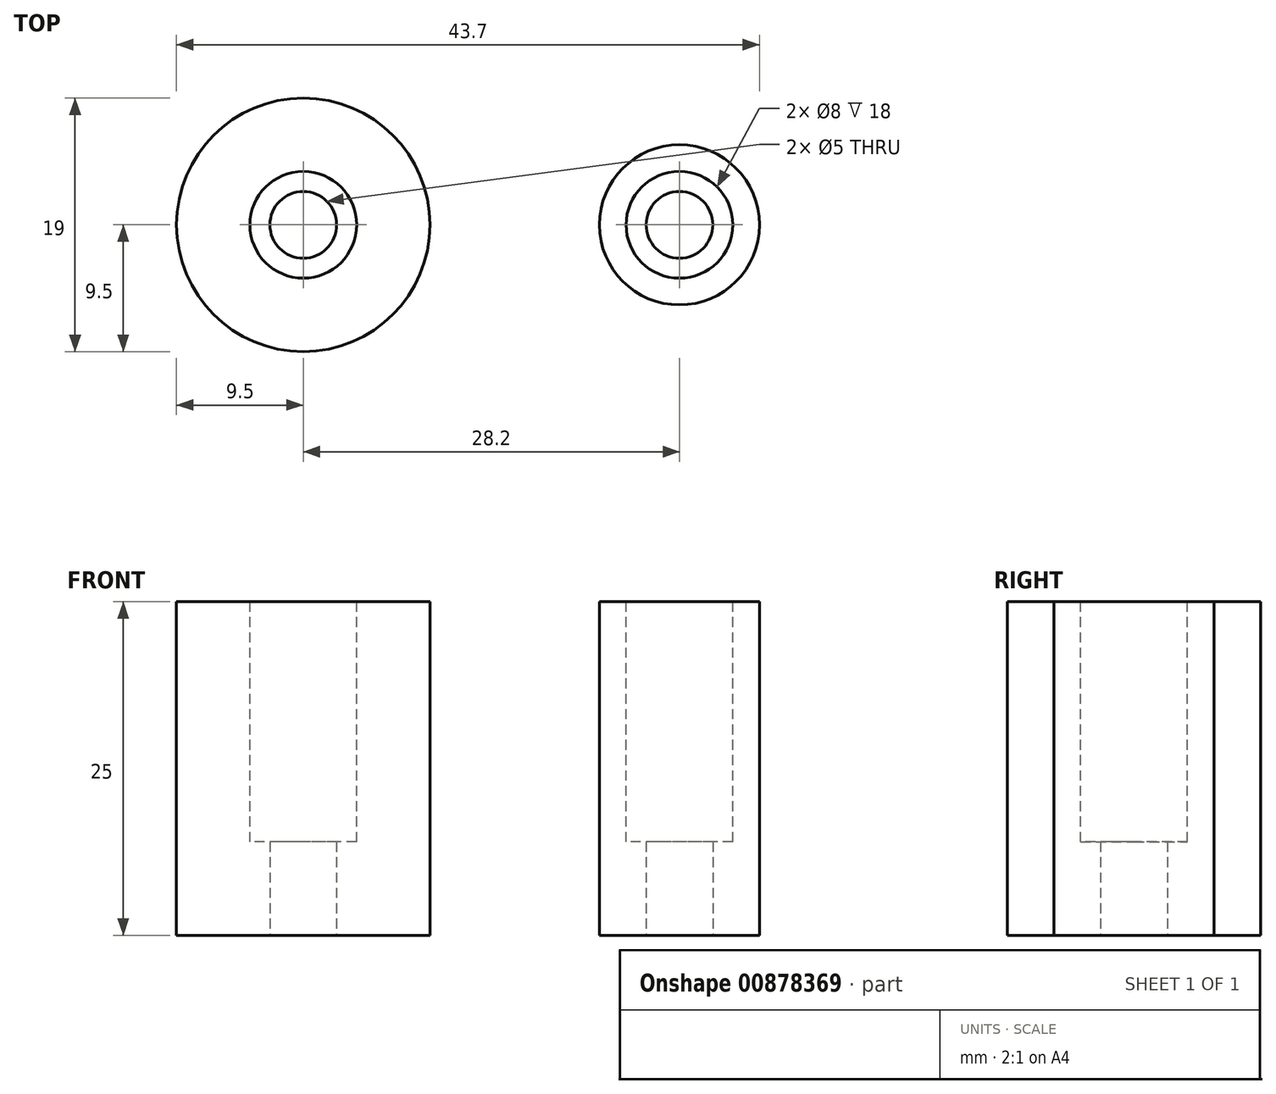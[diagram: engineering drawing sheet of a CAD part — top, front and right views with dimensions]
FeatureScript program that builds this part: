
annotation { "Feature Type Name" : "Feature", "Feature Type Description" : "" }
export const myFeature = defineFeature(function(context is Context, id is Id, definition is map)
    precondition{}
    {
        {
            var Q0;
            Q0=qCreatedBy(makeId("Top.planeOp"),FACE);
            var sketch = newSketch(context, id + "F0", { "sketchPlane" : qUnion([Q0])});
            skCircle(sketch, "E0", {"center": v(0, 0) * mm, "radius": 9.5 * mm});
            skSolve(sketch);
        }
        {
            var Q0;
            Q0 = qSketchRegion(id + "F0", true);
            extrude(context, id + "F1", {"entities" : qUnion([Q0]), "depth" : 25 * mm, "offsetDistance" : 25 * mm});
        }
        {
            var Q0;
            Q0=makeQuery(id+"F1.opExtrude","CAP_FACE",FACE,{"disambiguationData":[OSD([sQuery(id+"F0.wireOp",EDGE,"E0")])],"isStart":false});
            var sketch = newSketch(context, id + "F2", { "sketchPlane" : qUnion([Q0])});
            skCircle(sketch, "E1", {"center": v(0, 0) * mm, "radius": 4 * mm});
            skSolve(sketch);
        }
        {
            var Q0;
            Q0 = qSketchRegion(id + "F2", true);
            extrude(context, id + "F3", {"entities" : qUnion([Q0]), "operationType" : NewBodyOperationType.REMOVE, "oppositeDirection" : true, "depth" : 18 * mm, "offsetDistance" : 25 * mm});
        }
        {
            var Q0;
            Q0=makeQuery(id+"F1.opExtrude","CAP_FACE",FACE,{"disambiguationData":[OSD([sQuery(id+"F0.wireOp",EDGE,"E0")])],"isStart":true});
            var sketch = newSketch(context, id + "F4", { "sketchPlane" : qUnion([Q0])});
            skCircle(sketch, "E2", {"center": v(0, 0) * mm, "radius": 2.5 * mm});
            skSolve(sketch);
        }
        {
            var Q0;
            Q0 = qSketchRegion(id + "F4", true);
            extrude(context, id + "F5", {"entities" : qUnion([Q0]), "operationType" : NewBodyOperationType.REMOVE, "oppositeDirection" : true, "depth" : 25 * mm, "offsetDistance" : 25 * mm});
        }
        {
            var Q0;
            Q0=makeQuery(id+"F1.opExtrude","SWEPT_BODY",BODY,{"disambiguationData":[OSD([sQuery(id+"F0.wireOp",EDGE,"E0")])]});
            transform(context, id + "F6", {"entities" : qUnion([Q0]), "transformType" : TransformType.TRANSLATION_3D, "dx" : 28.2 * mm, "dy" : 0 * mm, "dz" : 0 * mm, "makeCopy" : true});
        }
        {
            var Q0;
            Q0=makeQuery(id+"F6.opPattern","COPY",FACE,{"derivedFrom":makeQuery(id+"F1.opExtrude","CAP_FACE",FACE,{"disambiguationData":[OSD([sQuery(id+"F0.wireOp",EDGE,"E0")])],"isStart":false}),"instanceName":"1"});
            var sketch = newSketch(context, id + "F7", { "sketchPlane" : qUnion([Q0])});
            skCircle(sketch, "E3", {"center": v(28.2, 0) * mm, "radius": 6 * mm});
            skSolve(sketch);
        }
        {
            var Q0;
            Q0=makeQuery(id+"F7.imprint","IMPRINT",FACE,{"disambiguationData":[TD([[makeQuery(id+"F7.imprint","IMPRINT",EDGE,{"derivedFrom":sQuery(id+"F7.wireOp",EDGE,"E3")}),-1.0]])]});
            extrude(context, id + "F8", {"entities" : qUnion([Q0]), "operationType" : NewBodyOperationType.REMOVE, "oppositeDirection" : true, "depth" : 25 * mm, "offsetDistance" : 25 * mm});
        }
    });
